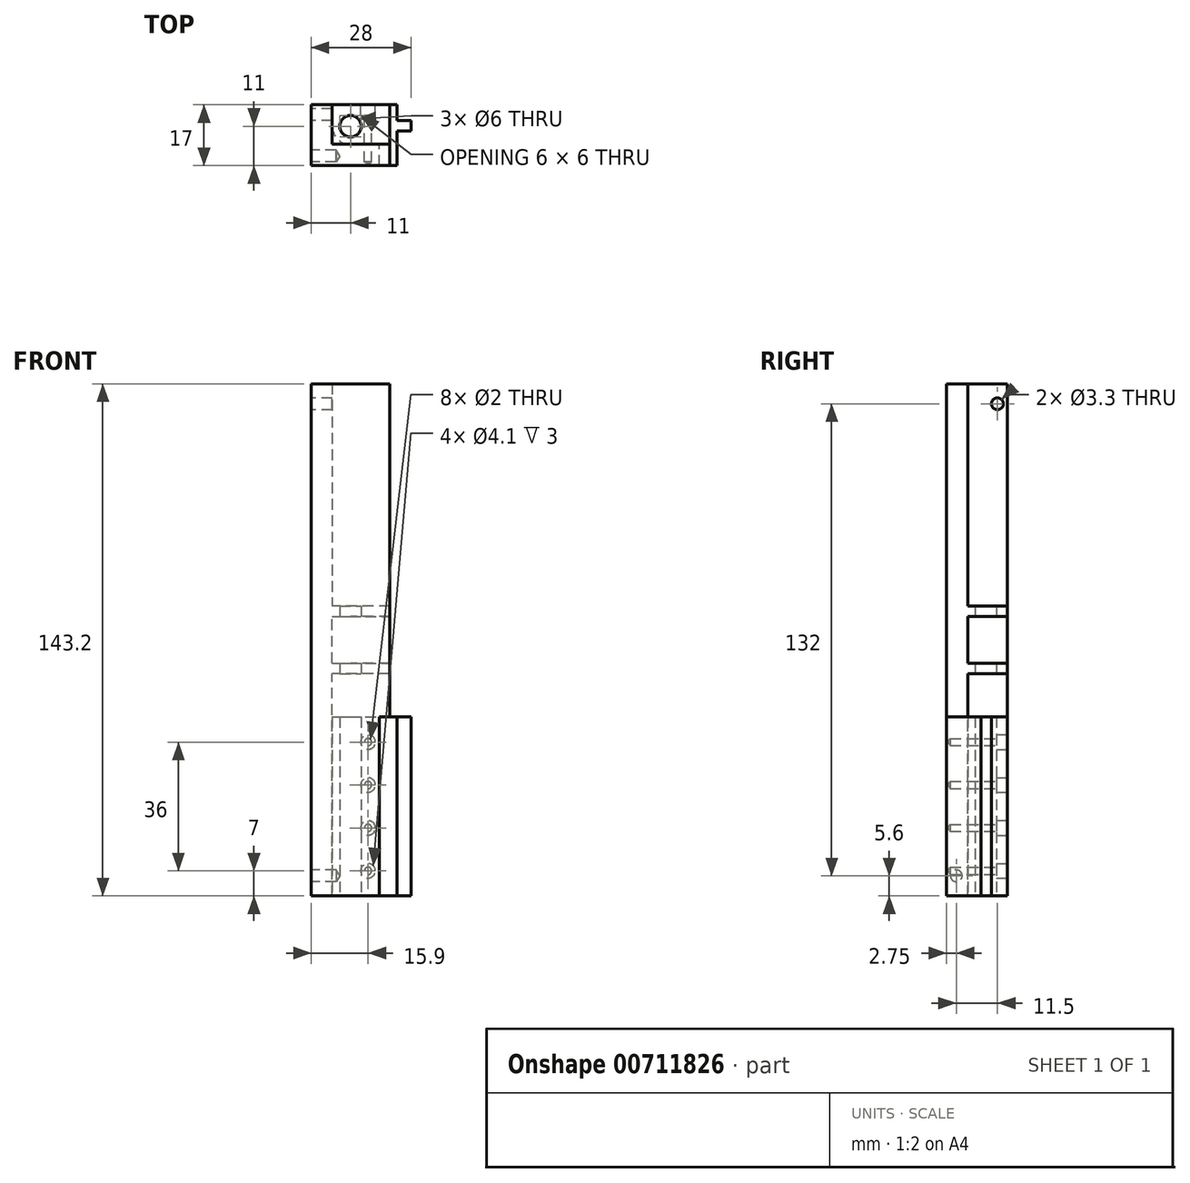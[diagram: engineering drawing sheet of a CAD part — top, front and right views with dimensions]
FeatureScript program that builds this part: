
annotation { "Feature Type Name" : "Feature", "Feature Type Description" : "" }
export const myFeature = defineFeature(function(context is Context, id is Id, definition is map)
    precondition{}
    {
        {
            var Q0;
            Q0=qCreatedBy(makeId("Top.planeOp"),FACE);
            var sketch = newSketch(context, id + "F0", { "sketchPlane" : qUnion([Q0])});
            skLineSegment(sketch, "E0.bottom", {"start": v(0, 0) * mm, "end": v(22, 0) * mm});
            skLineSegment(sketch, "E0.top", {"start": v(0, 17) * mm, "end": v(22, 17) * mm});
            skLineSegment(sketch, "E0.left", {"start": v(0, 0) * mm, "end": v(0, 17) * mm});
            skLineSegment(sketch, "E0.right", {"start": v(22, 0) * mm, "end": v(22, 17) * mm});
            skCircle(sketch, "E1", {"center": v(11, 11) * mm, "radius": 3 * mm});
            skSolve(sketch);
        }
        {
            var Q0;
            Q0 = qSketchRegion(id + "F0", true);
            extrude(context, id + "F1", {"entities" : qUnion([Q0]), "endBound" : BoundingType.SYMMETRIC, "depth" : 143.2 * mm, "offsetDistance" : 25 * mm});
        }
        {
            var Q0;
            Q0=qCreatedBy(makeId("Top.planeOp"),FACE);
            var sketch = newSketch(context, id + "F2", { "sketchPlane" : qUnion([Q0])});
            skCircle(sketch, "E2", {"center": v(11, 11) * mm, "radius": 5.1 * mm});
            skLineSegment(sketch, "E3", {"start": v(5.9, 11) * mm, "end": v(5.9, 17) * mm});
            skLineSegment(sketch, "E4", {"start": v(5.9, 17) * mm, "end": v(22, 17) * mm});
            skLineSegment(sketch, "E5", {"start": v(22, 17) * mm, "end": v(22, 5.9) * mm});
            skLineSegment(sketch, "E6", {"start": v(22, 5.9) * mm, "end": v(11, 5.9) * mm});
            skSolve(sketch);
        }
        {
            var Q0;
            Q0 = qSketchRegion(id + "F2", true);
            extrude(context, id + "F3", {"entities" : qUnion([Q0]), "operationType" : NewBodyOperationType.REMOVE, "endBound" : BoundingType.SYMMETRIC, "oppositeDirection" : true, "depth" : 13 * mm, "offsetDistance" : 25 * mm});
        }
        {
            var Q0;
            Q0=makeQuery(id+"F1.opExtrude","SWEPT_FACE",FACE,{"disambiguationData":[OSD([sQuery(id+"F0.wireOp",EDGE,"E0.top")])]});
            var sketch = newSketch(context, id + "F4", { "sketchPlane" : qUnion([Q0])});
            skLineSegment(sketch, "E7.bottom", {"start": v(-22, -71.6) * mm, "end": v(-5.9, -71.6) * mm});
            skLineSegment(sketch, "E7.top", {"start": v(-22, -9.5) * mm, "end": v(-5.9, -9.5) * mm});
            skLineSegment(sketch, "E7.left", {"start": v(-22, -71.6) * mm, "end": v(-22, -9.5) * mm});
            skLineSegment(sketch, "E7.right", {"start": v(-5.9, -71.6) * mm, "end": v(-5.9, -9.5) * mm});
            skLineSegment(sketch, "E8.bottom", {"start": v(-22, 71.6) * mm, "end": v(-5.9, 71.6) * mm});
            skLineSegment(sketch, "E8.top", {"start": v(-22, 9.5) * mm, "end": v(-5.9, 9.5) * mm});
            skLineSegment(sketch, "E8.left", {"start": v(-22, 71.6) * mm, "end": v(-22, 9.5) * mm});
            skLineSegment(sketch, "E8.right", {"start": v(-5.9, 71.6) * mm, "end": v(-5.9, 9.5) * mm});
            skLineSegment(sketch, "E9", {"start": v(-5.9, -9.5) * mm, "end": v(-5.9, 9.5) * mm, "construction": true});
            skSolve(sketch);
        }
        {
            var Q0;
            Q0 = qSketchRegion(id + "F4", true);
            extrude(context, id + "F5", {"entities" : qUnion([Q0]), "operationType" : NewBodyOperationType.REMOVE, "oppositeDirection" : true, "depth" : 11 * mm, "offsetDistance" : 25 * mm});
        }
        {
            var Q0;
            Q0=makeQuery(id+"F5.boolean.opBoolean","COPY",FACE,{"derivedFrom":makeQuery(id+"F5.opExtrude","CAP_FACE",FACE,{"disambiguationData":[OSD([sQuery(id+"F4.wireOp",EDGE,"E7.bottom"),sQuery(id+"F4.wireOp",EDGE,"E7.top"),sQuery(id+"F4.wireOp",EDGE,"E7.left"),sQuery(id+"F4.wireOp",EDGE,"E7.right")])],"isStart":false})});
            var sketch = newSketch(context, id + "F6", { "sketchPlane" : qUnion([Q0])});
            skLineSegment(sketch, "E10.bottom", {"start": v(-22, -21.6) * mm, "end": v(-19, -21.6) * mm});
            skLineSegment(sketch, "E10.top", {"start": v(-22, -71.6) * mm, "end": v(-19, -71.6) * mm});
            skLineSegment(sketch, "E10.left", {"start": v(-22, -21.6) * mm, "end": v(-22, -71.6) * mm});
            skLineSegment(sketch, "E10.right", {"start": v(-19, -21.6) * mm, "end": v(-19, -71.6) * mm});
            skSolve(sketch);
        }
        {
            var Q0;
            Q0 = qSketchRegion(id + "F6", true);
            extrude(context, id + "F7", {"entities" : qUnion([Q0]), "operationType" : NewBodyOperationType.REMOVE, "oppositeDirection" : true, "depth" : 25 * mm, "offsetDistance" : 25 * mm});
        }
        {
            var Q0;
            Q0=makeQuery(id+"F1.opExtrude","SWEPT_FACE",FACE,{"disambiguationData":[OSD([sQuery(id+"F0.wireOp",EDGE,"E0.left")])]});
            var sketch = newSketch(context, id + "F8", { "sketchPlane" : qUnion([Q0])});
            skLineSegment(sketch, "E11.bottom", {"start": v(-2.75, -66) * mm, "end": v(-14.25, -66) * mm, "construction": true});
            skLineSegment(sketch, "E11.top", {"start": v(-2.75, 66) * mm, "end": v(-14.25, 66) * mm, "construction": true});
            skLineSegment(sketch, "E11.left", {"start": v(-2.75, -66) * mm, "end": v(-2.75, 66) * mm, "construction": true});
            skLineSegment(sketch, "E11.right", {"start": v(-14.25, -66) * mm, "end": v(-14.25, 66) * mm, "construction": true});
            skPoint(sketch, "E12", {"position": v(-2.75, -66) * mm});
            skPoint(sketch, "E13", {"position": v(-14.25, 66) * mm});
            skSolve(sketch);
        }
        {
            var Q0;
            Q0=sQuery(id+"F8.wireOp",VERTEX,"E11.bottom.start");
            var Q1;
            Q1=sQuery(id+"F8.wireOp",VERTEX,"E11.right.end");
            var Q2;
            Q2=makeQuery(id+"F1.opExtrude","SWEPT_BODY",BODY,{"disambiguationData":[OSD([sQuery(id+"F0.wireOp",EDGE,"E0.bottom"),sQuery(id+"F0.wireOp",EDGE,"E0.top"),sQuery(id+"F0.wireOp",EDGE,"E0.left"),sQuery(id+"F0.wireOp",EDGE,"E0.right"),sQuery(id+"F0.wireOp",EDGE,"E1")])]});
            hole(context, id + "F9", {"style" : HoleStyle.SIMPLE, "endStyle" : HoleEndStyle.BLIND, "standardTappedOrClearance" : lookupTablePath({ "standard" : "ISO", "fit" : "Normal", "size" : "M3", "type" : "Clearance" }), "standardBlindInLast" : lookupTablePath({ "fit" : "Standard", "standard" : "ISO", "size" : "M3", "type" : "Clearance" }), "holeDiameter" : 3.3 * mm, "majorDiameter" : 5 * mm, "holeDepth" : 7 * mm, "isTappedThrough" : true, "tappedDepth" : 7 * mm, "tapClearance" : 2, "startFromSketch" : true, "locations" : qUnion([Q0, Q1]), "scope" : qUnion([Q2])});
        }
        {
            var Q0;
            Q0=makeQuery(id+"F1.opExtrude","CAP_FACE",FACE,{"disambiguationData":[OSD([sQuery(id+"F0.wireOp",EDGE,"E0.bottom"),sQuery(id+"F0.wireOp",EDGE,"E0.top"),sQuery(id+"F0.wireOp",EDGE,"E0.left"),sQuery(id+"F0.wireOp",EDGE,"E0.right"),sQuery(id+"F0.wireOp",EDGE,"E1")])],"isStart":true});
            var sketch = newSketch(context, id + "F10", { "sketchPlane" : qUnion([Q0])});
            skLineSegment(sketch, "E14.bottom", {"start": v(5.9, -6) * mm, "end": v(24, -6) * mm});
            skLineSegment(sketch, "E14.top", {"start": v(5.9, -17) * mm, "end": v(24, -17) * mm});
            skLineSegment(sketch, "E14.left", {"start": v(5.9, -6) * mm, "end": v(5.9, -17) * mm});
            skLineSegment(sketch, "E14.right", {"start": v(24, -6) * mm, "end": v(24, -17) * mm});
            skLineSegment(sketch, "E15.bottom", {"start": v(24, -9.63) * mm, "end": v(28, -9.63) * mm});
            skLineSegment(sketch, "E15.top", {"start": v(24, -12.63) * mm, "end": v(28, -12.63) * mm});
            skLineSegment(sketch, "E15.left", {"start": v(24, -9.63) * mm, "end": v(24, -12.63) * mm});
            skLineSegment(sketch, "E15.right", {"start": v(28, -9.63) * mm, "end": v(28, -12.63) * mm});
            skLineSegment(sketch, "E16.bottom", {"start": v(24, -6) * mm, "end": v(19, -6) * mm});
            skLineSegment(sketch, "E16.top", {"start": v(24, 0) * mm, "end": v(19, 0) * mm});
            skLineSegment(sketch, "E16.left", {"start": v(24, -6) * mm, "end": v(24, 0) * mm});
            skLineSegment(sketch, "E16.right", {"start": v(19, -6) * mm, "end": v(19, 0) * mm});
            skCircle(sketch, "E17", {"center": v(11, -11) * mm, "radius": 3 * mm});
            skSolve(sketch);
        }
        {
            var Q0;
            Q0 = qSketchRegion(id + "F10", true);
            extrude(context, id + "F11", {"entities" : qUnion([Q0]), "oppositeDirection" : true, "depth" : 50 * mm, "offsetDistance" : 25 * mm});
        }
        {
            var Q0;
            Q0=makeQuery(id+"F11.opExtrude","SWEPT_FACE",FACE,{"disambiguationData":[OSD([sQuery(id+"F10.wireOp",EDGE,"E14.top")])]});
            var sketch = newSketch(context, id + "F12", { "sketchPlane" : qUnion([Q0])});
            skLineSegment(sketch, "E18", {"start": v(-15.9, -21.6) * mm, "end": v(-15.9, -71.6) * mm, "construction": true});
            skPoint(sketch, "E19", {"position": v(-15.9, -28.6) * mm});
            skPoint(sketch, "E20", {"position": v(-15.9, -64.6) * mm});
            skPoint(sketch, "E21", {"position": v(-15.9, -52.6) * mm});
            skPoint(sketch, "E22", {"position": v(-15.9, -40.6) * mm});
            skSolve(sketch);
        }
        {
            var Q0;
            Q0=sQuery(id+"F12.wireOp",VERTEX,"E20");
            var Q1;
            Q1=sQuery(id+"F12.wireOp",VERTEX,"E21");
            var Q2;
            Q2=sQuery(id+"F12.wireOp",VERTEX,"E22");
            var Q3;
            Q3=sQuery(id+"F12.wireOp",VERTEX,"E19");
            var Q4;
            Q4=makeQuery(id+"F1.opExtrude","SWEPT_BODY",BODY,{"disambiguationData":[OSD([sQuery(id+"F0.wireOp",EDGE,"E0.bottom"),sQuery(id+"F0.wireOp",EDGE,"E0.top"),sQuery(id+"F0.wireOp",EDGE,"E0.left"),sQuery(id+"F0.wireOp",EDGE,"E0.right"),sQuery(id+"F0.wireOp",EDGE,"E1")])]});
            var Q5;
            Q5=makeQuery(id+"F11.opExtrude","SWEPT_BODY",BODY,{"disambiguationData":[OSD([sQuery(id+"F10.wireOp",EDGE,"E14.bottom"),sQuery(id+"F10.wireOp",EDGE,"E14.top"),sQuery(id+"F10.wireOp",EDGE,"E14.left"),sQuery(id+"F10.wireOp",EDGE,"E14.right"),sQuery(id+"F10.wireOp",EDGE,"E15.bottom"),sQuery(id+"F10.wireOp",EDGE,"E15.top"),sQuery(id+"F10.wireOp",EDGE,"E15.right"),sQuery(id+"F10.wireOp",EDGE,"E16.top"),sQuery(id+"F10.wireOp",EDGE,"E16.left"),sQuery(id+"F10.wireOp",EDGE,"E16.right"),sQuery(id+"F10.wireOp",EDGE,"E17")])]});
            hole(context, id + "F13", {"style" : HoleStyle.C_BORE, "endStyle" : HoleEndStyle.BLIND, "holeDiameter" : 2 * mm, "cBoreDiameter" : 4.1 * mm, "cBoreDepth" : 3 * mm, "majorDiameter" : 5 * mm, "holeDepth" : 16 * mm, "isTappedThrough" : true, "tappedDepth" : 7 * mm, "tapClearance" : 2, "startFromSketch" : true, "locations" : qUnion([Q0, Q1, Q2, Q3]), "scope" : qUnion([Q4, Q5])});
        }
    });
